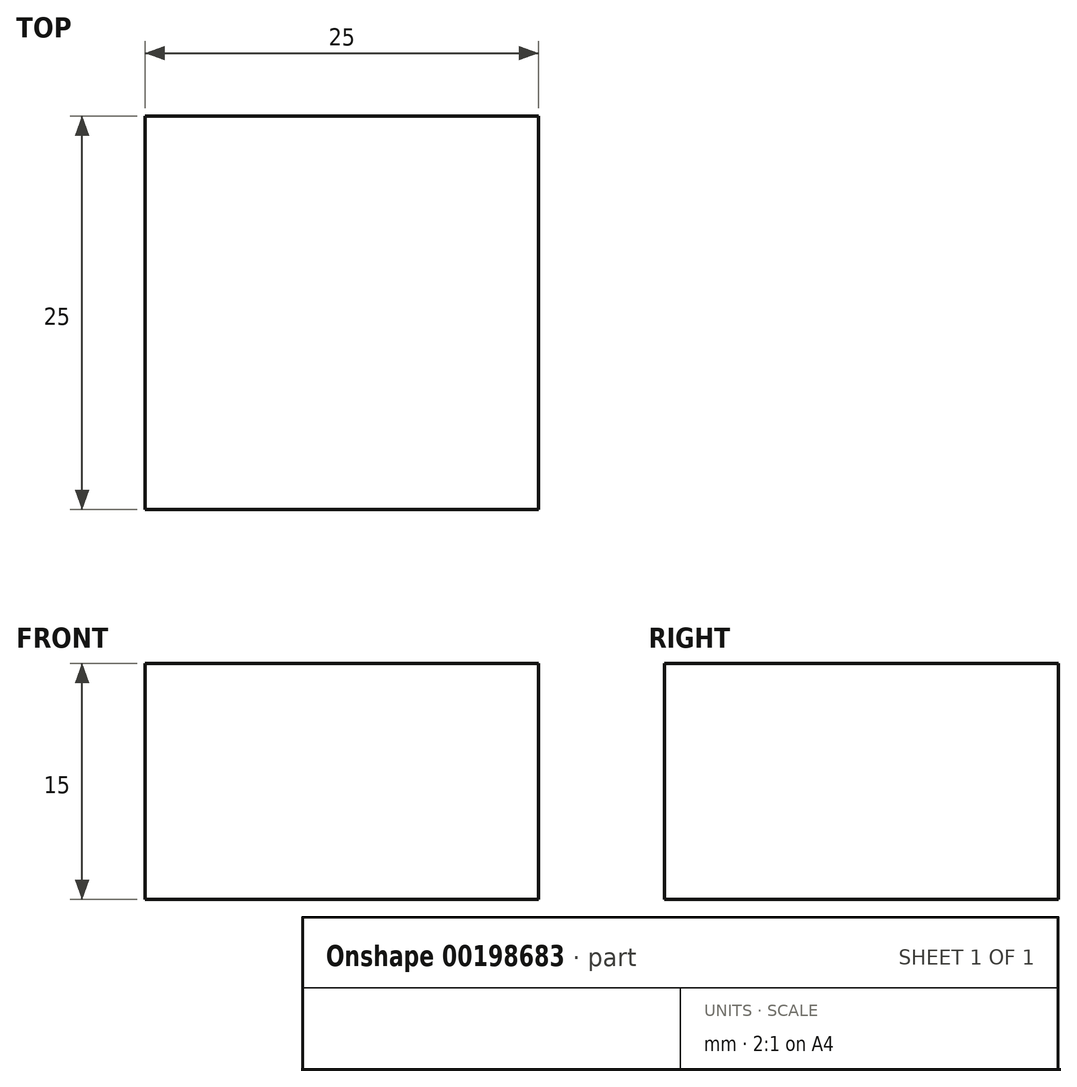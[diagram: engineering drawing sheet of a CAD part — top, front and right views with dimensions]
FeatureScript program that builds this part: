
annotation { "Feature Type Name" : "Feature", "Feature Type Description" : "" }
export const myFeature = defineFeature(function(context is Context, id is Id, definition is map)
    precondition{}
    {
        {
            var Q0;
            Q0=qCreatedBy(makeId("Top.planeOp"),FACE);
            var sketch = newSketch(context, id + "F0", { "sketchPlane" : qUnion([Q0])});
            skLineSegment(sketch, "E0.bottom", {"start": v(12.5, -12.5) * mm, "end": v(-12.5, -12.5) * mm});
            skLineSegment(sketch, "E0.top", {"start": v(12.5, 12.5) * mm, "end": v(-12.5, 12.5) * mm});
            skLineSegment(sketch, "E0.left", {"start": v(12.5, -12.5) * mm, "end": v(12.5, 12.5) * mm});
            skLineSegment(sketch, "E0.right", {"start": v(-12.5, -12.5) * mm, "end": v(-12.5, 12.5) * mm});
            skPoint(sketch, "E0.middle", {"position": v(0, 0) * mm});
            skSolve(sketch);
        }
        {
            var Q0;
            Q0 = qSketchRegion(id + "F0", true);
            extrude(context, id + "F1", {"entities" : qUnion([Q0]), "depth" : 15 * mm});
        }
    });
